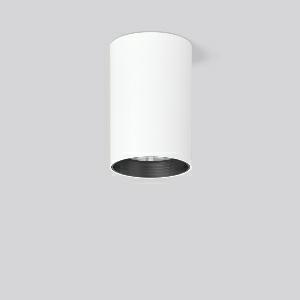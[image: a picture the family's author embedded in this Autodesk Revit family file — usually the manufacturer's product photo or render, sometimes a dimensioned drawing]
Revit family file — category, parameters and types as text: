
# Revit family: heledon_maxi_a_931221_002_1_9b30
name_source: partatom
category: Lighting Fixtures
units: mm (PartAtom-declared; Revit-internal decimal feet)

## family parameters
Cut with Voids When Loaded = No
Host = Face
Light Source = No
Part Type = Normal
Room Calculation Point = No
Round Connector Dimension = Use Diameter
Shared = No

## types (1)
- HELEDON maxi A (1 x LED Modul 940, 2850 lm, 4000)
    Apparent Load = 25 VA
    Approval mark = CE
    CIE Flux Codes = 96 100 100 100 100
    Color Rendering = 92
    Color Temperature = 4000
    Default Elevation = 1800 mm
    Description = Series: HELEDON maxi
Cylindrical surface-mounted downlight. Housing: die-cast aluminium, powder-coated. Internal ceiling frame polycarbonate with bayonet mounting. Black plastic ring and recessed LED to prevent glare from the side. Optical assembly with lens made of plastic (polycarbonate) for the best homogeneous light distribution - can be changed without tools. Best colour rendering index Ra>90. Suitable for Ceiling mounting. Easy installation with a separate ceiling frame with bayonet mounting and plug connection. Driver integrated. Connected via plug-in connector. High quality converter without flickering and stroboscopic effect. The following accessories can be mounted without use of tools: interchangeable lenses, decorative glasses, honeycomb louvre, clear and frosted diffusers, white interchangeable plastic ring. 
Colour: traffic white, matt (RAL 9016)
Diameter: 123 mm
Height: 183 mm
Lamp: LED
Socket: without socket
Colour temperature: 4000K
Colour rendering index (CRI): 92
System power: 25 W
Rated luminous flux: 2850 lm
Luminous efficiency: 114 lm/W
Control gear: Regulated power supply
Protection class: I
Type of protection: IP 20
    Height = 183 mm
    Lamp = 1 x LED Modul 940
    Lamp Light Flux = 2850 lm
    Lamp count = 1
    Length = 123 mm
    Lifetime = 50000 h
    Luminous efficacy = 114 lm/W
    Manufacturer = RZB
    ModVariant = No
    Model = 931221.002.1
    Mounting Place = Ceiling
    Mounting Type = Surface mounted
    Number of Poles = 1
    OnlyDefault = Yes
    Power Factor = 1
    Product Name = HELEDON maxi A
    Product group = Surface mounted downlights
    ProductGroupID = 302
    Protection Class = Protection class I
    Protection Degree = IP 20
    RLX_Detail_Level = 1
    RLX_Emergency_Light_Flux = 0 lm
    RLX_Emergency_Type = 0
    RLX_Emergency_Type_DB = No
    RlxData = <blob elided: 96249 chars, md5=ff52ca13>
    Socket = socket
    Standby Power = 0 W
    System Light Flux = 2850 lm
    System Power = 25 W
    Type Comments = Product without accessories
    Type Image = 931193.002.jpg
    URL = http://relux.com
    VarID = ---
    Voltage = 230 V
    Voltage Range = 220-240 V
    Weight = 0.00 kg
    Width = 0 mm  [stored 0 ft]

note: [stored X ft] marks values corroborated as IEEE doubles in the binary element streams (Revit-internal decimal feet)

## geometry (parser evidence)
native form markers: Blend x4, Sweep x13
no freeform markers — native parametric forms only
